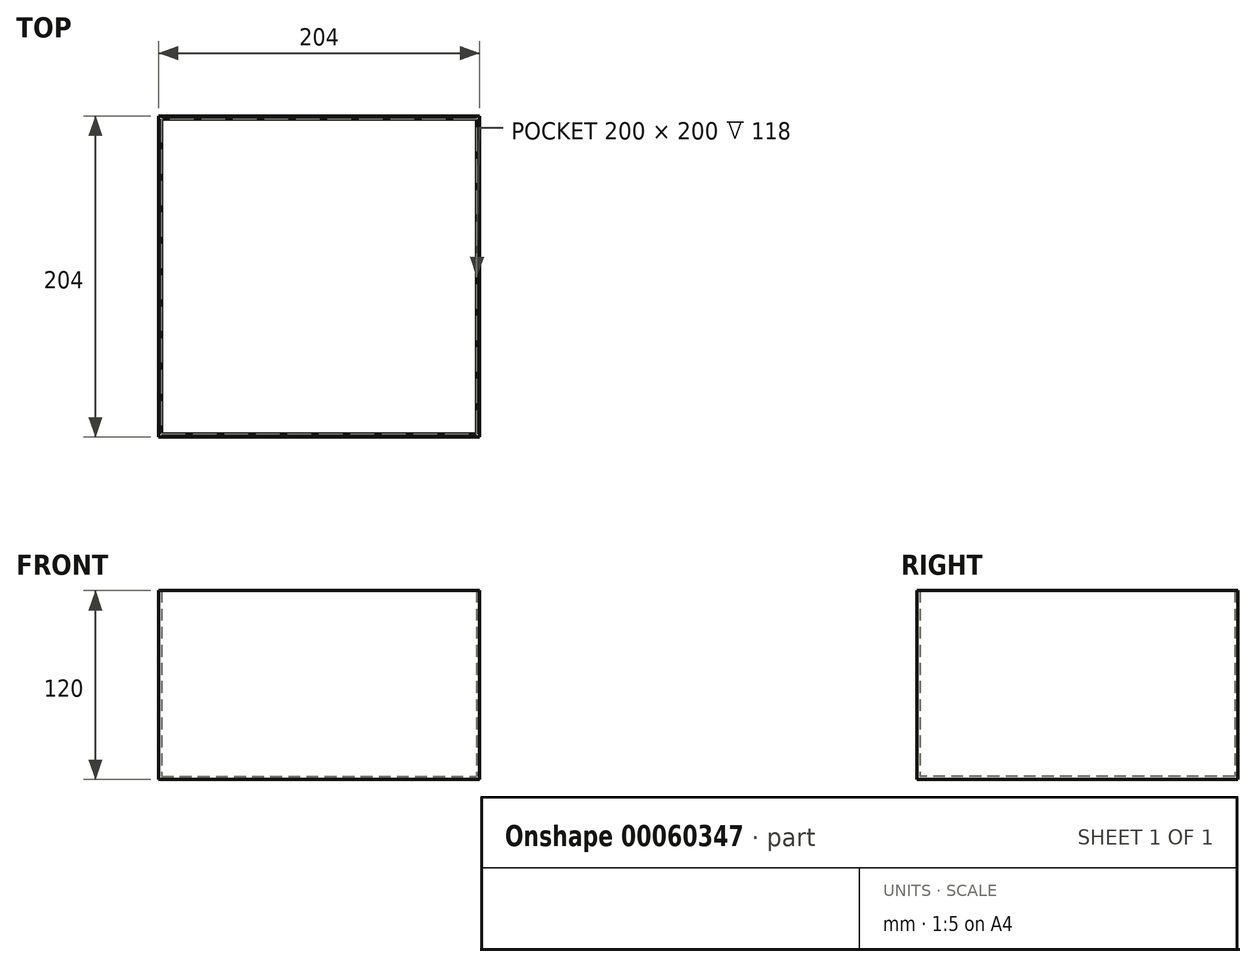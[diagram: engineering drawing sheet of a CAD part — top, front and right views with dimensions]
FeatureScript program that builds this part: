
annotation { "Feature Type Name" : "Feature", "Feature Type Description" : "" }
export const myFeature = defineFeature(function(context is Context, id is Id, definition is map)
    precondition{}
    {
        {
            assignVariable(context, id + "F0", {"name" : "WallThickness", "anyValue" : 2});
        }
        {
            assignVariable(context, id + "F1", {"name" : "BottomHeight", "anyValue" : 120});
        }
        {
            var Q0;
            Q0=qCreatedBy(makeId("Top.planeOp"),FACE);
            var sketch = newSketch(context, id + "F2", { "sketchPlane" : qUnion([Q0])});
            skLineSegment(sketch, "E0.bottom", {"start": v(-102, 102) * mm, "end": v(102, 102) * mm});
            skLineSegment(sketch, "E0.top", {"start": v(-102, -102) * mm, "end": v(102, -102) * mm});
            skLineSegment(sketch, "E0.left", {"start": v(-102, 102) * mm, "end": v(-102, -102) * mm});
            skLineSegment(sketch, "E0.right", {"start": v(102, 102) * mm, "end": v(102, -102) * mm});
            skSolve(sketch);
        }
        {
            var Q0;
            Q0 = qSketchRegion(id + "F2", true);
            extrude(context, id + "F3", {"entities" : qUnion([Q0]), "depth" : (getVariable(context, 'BottomHeight')) * mm});
        }
        {
            var Q0;
            Q0=makeQuery(id+"F3.opExtrude","CAP_FACE",FACE,{"disambiguationData":[OSD([sQuery(id+"F2.wireOp",EDGE,"E0.bottom"),sQuery(id+"F2.wireOp",EDGE,"E0.top"),sQuery(id+"F2.wireOp",EDGE,"E0.left"),sQuery(id+"F2.wireOp",EDGE,"E0.right")])],"isStart":false});
            shell(context, id + "F4", {"entities" : qUnion([Q0]), "thickness" : (getVariable(context, 'WallThickness')) * mm});
        }
    });
